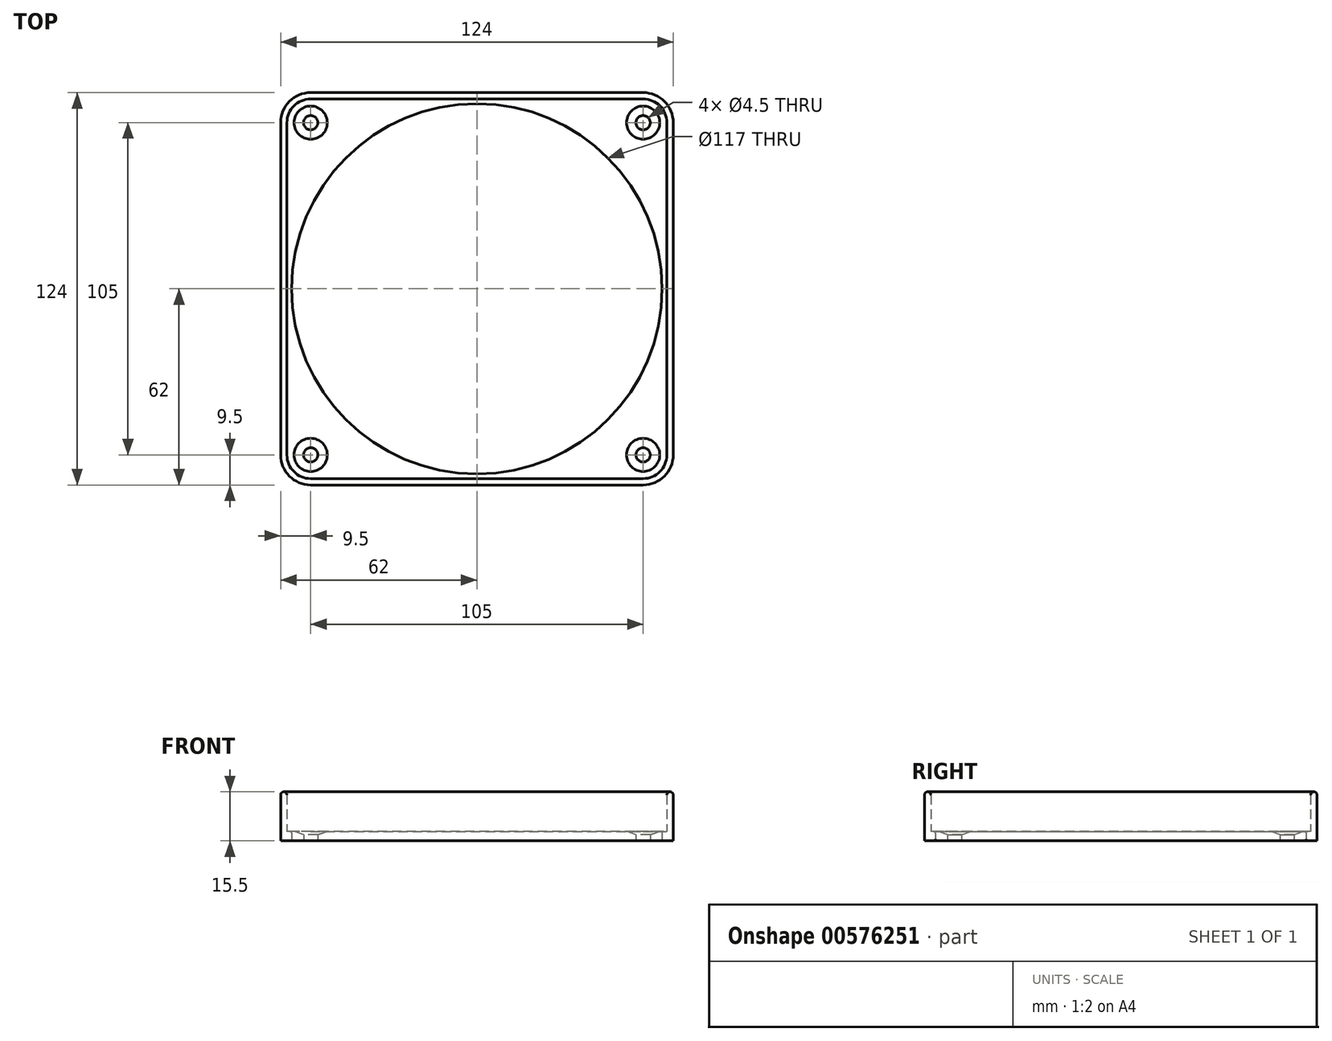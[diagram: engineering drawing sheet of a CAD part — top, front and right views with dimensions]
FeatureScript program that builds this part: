
annotation { "Feature Type Name" : "Feature", "Feature Type Description" : "" }
export const myFeature = defineFeature(function(context is Context, id is Id, definition is map)
    precondition{}
    {
        {
            var Q0;
            Q0=qCreatedBy(makeId("Top.planeOp"),FACE);
            var sketch = newSketch(context, id + "F0", { "sketchPlane" : qUnion([Q0])});
            skCircle(sketch, "E0", {"center": v(52.5, 52.5) * mm, "radius": 2.25 * mm});
            skLineSegment(sketch, "E1.0", {"start": v(-52.5, 60) * mm, "end": v(52.5, 60) * mm});
            skLineSegment(sketch, "E1.1", {"start": v(-60, -52.5) * mm, "end": v(-60, 52.5) * mm});
            skLineSegment(sketch, "E1.2", {"start": v(-52.5, -60) * mm, "end": v(52.5, -60) * mm});
            skLineSegment(sketch, "E1.3", {"start": v(60, -52.5) * mm, "end": v(60, 52.5) * mm});
            skArc(sketch, "E2", {"start": v(52.5, 60) * mm, "mid": v(57.8, 57.8) * mm, "end": v(60, 52.5) * mm});
            skCircle(sketch, "E3.1.0", {"center": v(-52.5, 52.5) * mm, "radius": 2.25 * mm});
            skArc(sketch, "E3.1.1", {"start": v(-60, 52.5) * mm, "mid": v(-57.8, 57.8) * mm, "end": v(-52.5, 60) * mm});
            skCircle(sketch, "E3.2.0", {"center": v(-52.5, -52.5) * mm, "radius": 2.25 * mm});
            skArc(sketch, "E3.2.1", {"start": v(-52.5, -60) * mm, "mid": v(-57.8, -57.8) * mm, "end": v(-60, -52.5) * mm});
            skCircle(sketch, "E3.3.0", {"center": v(52.5, -52.5) * mm, "radius": 2.25 * mm});
            skArc(sketch, "E3.3.1", {"start": v(60, -52.5) * mm, "mid": v(57.8, -57.8) * mm, "end": v(52.5, -60) * mm});
            skPoint(sketch, "E3.center", {"position": v(0, 0) * mm});
            skCircle(sketch, "E4", {"center": v(0, 0) * mm, "radius": 58.5 * mm});
            skArc(sketch, "E5.0", {"start": v(-62, 52.5) * mm, "mid": v(-59.22, 59.22) * mm, "end": v(-52.5, 62) * mm});
            skLineSegment(sketch, "E5.1", {"start": v(-62, -52.5) * mm, "end": v(-62, 52.5) * mm});
            skLineSegment(sketch, "E5.2", {"start": v(-52.5, 62) * mm, "end": v(52.5, 62) * mm});
            skArc(sketch, "E5.3", {"start": v(-52.5, -62) * mm, "mid": v(-59.22, -59.22) * mm, "end": v(-62, -52.5) * mm});
            skArc(sketch, "E5.4", {"start": v(52.5, 62) * mm, "mid": v(59.22, 59.22) * mm, "end": v(62, 52.5) * mm});
            skLineSegment(sketch, "E5.5", {"start": v(62, -52.5) * mm, "end": v(62, 52.5) * mm});
            skArc(sketch, "E5.6", {"start": v(62, -52.5) * mm, "mid": v(59.22, -59.22) * mm, "end": v(52.5, -62) * mm});
            skLineSegment(sketch, "E5.7", {"start": v(-52.5, -62) * mm, "end": v(52.5, -62) * mm});
            skSolve(sketch);
        }
        {
            var Q0;
            Q0=makeQuery(id+"F0.imprint","IMPRINT",FACE,{"disambiguationData":[TD([[makeQuery(id+"F0.imprint","IMPRINT",EDGE,{"derivedFrom":sQuery(id+"F0.wireOp",EDGE,"E0")}),-1.0]])]});
            extrude(context, id + "F1", {"entities" : qUnion([Q0]), "depth" : 3 * mm, "offsetDistance" : 25 * mm});
        }
        {
            var Q0;
            Q0=makeQuery(id+"F0.imprint","IMPRINT",FACE,{"disambiguationData":[TD([[makeQuery(id+"F0.imprint","IMPRINT",EDGE,{"derivedFrom":sQuery(id+"F0.wireOp",EDGE,"E1.0")}),1.0]])]});
            extrude(context, id + "F2", {"entities" : qUnion([Q0]), "operationType" : NewBodyOperationType.ADD, "depth" : 15.5 * mm, "offsetDistance" : 25 * mm});
        }
        {
            var Q0;
            Q0=makeQuery(id+"F2.opExtrude","CAP_FACE",FACE,{"disambiguationData":[OSD([sQuery(id+"F0.wireOp",EDGE,"E1.0"),sQuery(id+"F0.wireOp",EDGE,"E1.1"),sQuery(id+"F0.wireOp",EDGE,"E1.2"),sQuery(id+"F0.wireOp",EDGE,"E1.3"),sQuery(id+"F0.wireOp",EDGE,"E2"),sQuery(id+"F0.wireOp",EDGE,"E3.1.1"),sQuery(id+"F0.wireOp",EDGE,"E3.2.1"),sQuery(id+"F0.wireOp",EDGE,"E3.3.1"),sQuery(id+"F0.wireOp",EDGE,"E5.0"),sQuery(id+"F0.wireOp",EDGE,"E5.1"),sQuery(id+"F0.wireOp",EDGE,"E5.2"),sQuery(id+"F0.wireOp",EDGE,"E5.3"),sQuery(id+"F0.wireOp",EDGE,"E5.4"),sQuery(id+"F0.wireOp",EDGE,"E5.5"),sQuery(id+"F0.wireOp",EDGE,"E5.6"),sQuery(id+"F0.wireOp",EDGE,"E5.7")])],"isStart":false});
            fillet(context, id + "F3", {"entities" : qUnion([Q0]), "radius" : 1 * mm, "tangentPropagation" : true, "allowEdgeOverflow" : false});
        }
        {
            var Q0;
            Q0=makeQuery(id+"F1.opExtrude","CAP_EDGE",EDGE,{"disambiguationData":[OSD([sQuery(id+"F0.wireOp",EDGE,"E3.1.0")])],"isStart":false});
            var Q1;
            Q1=makeQuery(id+"F1.opExtrude","CAP_EDGE",EDGE,{"disambiguationData":[OSD([sQuery(id+"F0.wireOp",EDGE,"E3.2.0")])],"isStart":false});
            var Q2;
            Q2=makeQuery(id+"F1.opExtrude","CAP_EDGE",EDGE,{"disambiguationData":[OSD([sQuery(id+"F0.wireOp",EDGE,"E0")])],"isStart":false});
            var Q3;
            Q3=makeQuery(id+"F1.opExtrude","CAP_EDGE",EDGE,{"disambiguationData":[OSD([sQuery(id+"F0.wireOp",EDGE,"E3.3.0")])],"isStart":false});
            chamfer(context, id + "F4", {"entities" : qUnion([Q0, Q1, Q2, Q3]), "chamferType" : ChamferType.TWO_OFFSETS, "width1" : 1 * mm, "oppositeDirection" : false, "width2" : 3 * mm});
        }
        {
            var Q0;
            Q0=makeQuery(id+"F1.opExtrude","CAP_EDGE",EDGE,{"disambiguationData":[OSD([sQuery(id+"F0.wireOp",EDGE,"E4")])],"isStart":false});
            fillet(context, id + "F5", {"entities" : qUnion([Q0]), "radius" : .5 * mm, "tangentPropagation" : true, "allowEdgeOverflow" : false});
        }
        {
            var Q0;
            Q0=makeQuery(id+"F1.opExtrude","CAP_EDGE",EDGE,{"disambiguationData":[OSD([sQuery(id+"F0.wireOp",EDGE,"E4")])],"isStart":true});
            fillet(context, id + "F6", {"entities" : qUnion([Q0]), "radius" : .5 * mm, "tangentPropagation" : true, "allowEdgeOverflow" : false});
        }
    });
